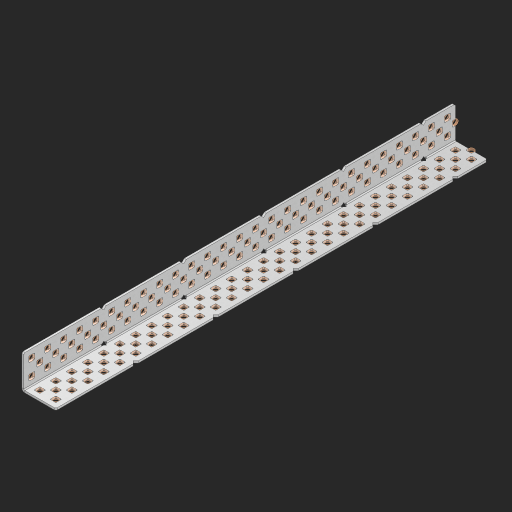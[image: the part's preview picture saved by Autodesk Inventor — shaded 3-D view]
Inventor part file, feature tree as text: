
AUTODESK INVENTOR PART (.ipt)
format: ipt  version: 2023 (Build 270158000, 158)  size: 1,927,168 bytes
history: native  units: in
note: dims shown in document units (in); Inventor stores cm internally (conversion verified against a paired STEP export)
features: other x168, extrude x160, sheet_metal_op x8, sketch x7, pattern_linear x2, mirror x1, chamfer x1
ambient origin geometry x8: Origin, YZ Plane, XZ Plane, XY Plane, X Axis, Y Axis, Z Axis, Center Point
bodies: Solid1 (feature_tree), Body (feature_tree)
feature tree (347):
  sheet_metal_op  "Flanges"
  sheet_metal_op  "Body Pattern"
  pattern_linear  "Center Pattern"  Spacing1=1.0in  [1 undecoded]
  other  "Arc Length"
  pattern_linear  "Notch Pattern"  Spacing1=0.25in  [1 undecoded]
  other  "Diagonal Plane"
  mirror  "Everything Mirrored"
  chamfer  "End Chamfer"
  sketch  "Sketch1"  dims[d0=1.0in]
  other  "Plate1"
  sketch  "Sketch2"  dims[d1=13.5in]
  other  "Plate2"
  sheet_metal_op  "Bend1"
  sheet_metal_op  "Corner1"
  sketch  "Sketch8"  dims[d2=0.0625in]
  sketch  "Sketch9"  dims[d3=0.0625in]
  other  "Srf91"
  sheet_metal_op  "Body Pattern Sketch"
  other  "Srf92"
  sketch  "Sketch13"  dims[d4=0.0312in]
  sketch  "Sketch15"  dims[d5=0.125in]
  sketch  "Sketch16"  dims[d6=0.0625in d7=1.0in d8=90.0deg d9=0.0312in d10=0.25in d11=0.0625in d12=0.0625in d49=0.182in d50=0.02in d52=0.25in d53=0.0625in d54=0.0in d55=0.172in d56=1.0in d57=0.0in d60=10.6299in d62=0.5in d63=0.7874in d65=0.5in d85=0.1473in d86=0.1782in d89=0.0625in d90=0.0in d91=0.04in d92=0.0491in d95=2.5in d96=0.04in d97=0.25in d98=45.0deg d99=0.25in d106=0.182in d107=0.02in d108=0.5in d110=0.0625in d111=0.0in d112=0.172in d113=0.5in d114=0.0in d117=0.5in d123=0.25in d125=0.25in d126=0.0491in d127=0.1473in d128=0.08in d129=0.04in d130=2.5in]
  other  "Srf786"
  other  "Srf856"
  other  "Srf857"
  other  "Srf858"
  other  "Srf859"
  other  "Srf860"
  other  "Srf861"
  other  "Srf889"
  other  "Srf890"
  other  "Srf891"
  other  "Srf1275"
  other  "Srf1276"
  other  "Srf1278"
  other  "Srf1279"
  other  "Srf1280"
  other  "Srf1281"
  other  "Srf1282"
  other  "Srf1283"
  other  "Srf1277"
  other  "Srf1285"
  other  "Srf1286"
  other  "Srf1287"
  other  "Srf1383"
  other  "Srf1384"
  other  "Srf1385"
  other  "Srf1386"
  other  "Srf1387"
  other  "Srf1388"
  other  "Srf1389"
  other  "Srf1390"
  other  "Srf1391"
  other  "Srf1392"
  other  "Srf1393"
  other  "Srf1394"
  other  "Srf1395"
  other  "Srf1396"
  other  "Srf1397"
  other  "Srf1398"
  other  "Srf1399"
  other  "Srf1400"
  other  "Srf1401"
  other  "Srf1402"
  other  "Srf1403"
  other  "Srf1404"
  other  "Srf1405"
  other  "Srf1406"
  other  "Srf1407"
  other  "Srf1408"
  other  "Srf1409"
  other  "Srf1410"
  other  "Srf1411"
  other  "Srf1412"
  other  "Srf1413"
  other  "Srf1414"
  other  "Srf1415"
  other  "Srf1416"
  other  "Srf1417"
  other  "Srf1418"
  other  "Srf1419"
  other  "Srf1420"
  other  "Srf1421"
  other  "Srf1422"
  other  "Srf1423"
  other  "Srf1424"
  other  "Srf1425"
  other  "Srf1426"
  other  "Srf1427"
  other  "Srf1428"
  other  "Srf1445"
  other  "Srf1446"
  other  "Srf1447"
  other  "Srf1448"
  other  "Srf1449"
  other  "Srf1450"
  other  "Srf1451"
  other  "Srf1452"
  other  "Srf1453"
  other  "Srf1454"
  other  "Srf1455"
  other  "Srf1456"
  other  "Srf1457"
  other  "Srf1458"
  other  "Srf1459"
  other  "Srf1460"
  other  "Srf1461"
  other  "Srf1462"
  other  "Srf1463"
  other  "Srf1464"
  other  "Srf1465"
  other  "Srf1466"
  other  "Srf1467"
  other  "Srf1475"
  other  "Srf1476"
  other  "Srf1477"
  other  "Srf1478"
  other  "Srf1479"
  other  "Srf1480"
  other  "Srf1481"
  other  "Srf1482"
  other  "Srf1483"
  other  "Srf1484"
  other  "Srf1485"
  other  "Srf1486"
  other  "Srf1487"
  other  "Srf1488"
  other  "Srf1489"
  other  "Srf1490"
  other  "Srf1491"
  other  "Srf1492"
  other  "Srf1493"
  other  "Srf1494"
  other  "Srf1495"
  other  "Srf1496"
  other  "Srf1497"
  other  "Srf1498"
  other  "Srf1499"
  other  "Srf1500"
  other  "Srf1501"
  other  "Srf1502"
  other  "Srf1503"
  other  "Srf1504"
  other  "Srf1505"
  other  "Srf1506"
  other  "Srf1507"
  other  "Srf1508"
  other  "Srf1509"
  other  "Srf1510"
  other  "Srf1511"
  other  "Srf1512"
  other  "Srf1513"
  other  "Srf1514"
  other  "Srf1515"
  other  "Srf1516"
  other  "Srf1517"
  other  "Srf1518"
  other  "Srf1519"
  other  "Srf1520"
  other  "Srf1537"
  other  "Srf1538"
  other  "Srf1539"
  other  "Srf1540"
  other  "Srf1541"
  other  "Srf1542"
  other  "Srf1543"
  other  "Srf1544"
  other  "Srf1545"
  other  "Srf1546"
  other  "Srf1547"
  other  "Srf1548"
  other  "Srf1549"
  other  "Srf1550"
  other  "Srf1551"
  other  "Srf1552"
  other  "Srf1553"
  other  "Srf1554"
  other  "Srf1555"
  other  "Srf1556"
  other  "Srf1557"
  other  "Srf1558"
  other  "Srf1559"
  sheet_metal_op  "Body Stamp"
  sheet_metal_op  "Body Circle"
  other  "Center Stamp"
  other  "Center Circle"
  sheet_metal_op  "Notch"
  extrude  "ExtrusionSrf92"  Depth=0.0625in
  extrude  "ExtrusionSrf856"  Depth=0.0625in
  extrude  "ExtrusionSrf857"  Depth=0.182in
  extrude  "ExtrusionSrf858"  Depth=0.02in
  extrude  "ExtrusionSrf859"  Depth=0.25in
  extrude  "ExtrusionSrf860"  Depth=0.0625in
  extrude  "ExtrusionSrf861"  TaperAngle=0.0deg  [1 undecoded]
  extrude  "ExtrusionSrf889"  Depth=2.5in
  extrude  "ExtrusionSrf890"  Depth=1.0in TaperAngle=0.0deg
  extrude  "ExtrusionSrf891"  Depth=2.5in
  extrude  "ExtrusionSrf1275"  Depth=0.5in
  extrude  "ExtrusionSrf1276"  Depth=2.5in
  extrude  "ExtrusionSrf1277"  Depth=2.5in
  extrude  "ExtrusionSrf1278"  Depth=0.0625in
  extrude  "ExtrusionSrf1279"  Depth=2.5in TaperAngle=0.0deg
  extrude  "ExtrusionSrf1280"  Depth=2.5in
  extrude  "ExtrusionSrf1281"  Depth=0.25in TaperAngle=45.0deg
  extrude  "ExtrusionSrf1282"  Depth=0.25in
  extrude  "ExtrusionSrf1345"  Depth=0.182in
  extrude  "ExtrusionSrf1346"  Depth=0.02in
  extrude  "ExtrusionSrf1347"  Depth=0.5in
  extrude  "ExtrusionSrf1348"  Depth=0.0625in
  extrude  "ExtrusionSrf1383"  TaperAngle=0.0deg  [1 undecoded]
  extrude  "ExtrusionSrf1384"  Depth=2.5in
  extrude  "ExtrusionSrf1385"  Depth=0.5in TaperAngle=0.0deg
  extrude  "ExtrusionSrf1386"  Depth=0.5in
  extrude  "ExtrusionSrf1387"  Depth=0.25in
  extrude  "ExtrusionSrf1388"  Depth=0.25in
  extrude  "ExtrusionSrf1389"  Depth=2.5in
  extrude  "ExtrusionSrf1390"  Depth=2.5in
  extrude  "ExtrusionSrf1391"  Depth=2.5in
  extrude  "ExtrusionSrf1392"  Depth=2.5in
  extrude  "ExtrusionSrf1393"  Depth=2.5in
  extrude  "ExtrusionSrf1394"  [1 undecoded]
  extrude  "ExtrusionSrf1395"  [1 undecoded]
  extrude  "ExtrusionSrf1396"  [1 undecoded]
  extrude  "ExtrusionSrf1397"  [1 undecoded]
  extrude  "ExtrusionSrf1398"  [1 undecoded]
  extrude  "ExtrusionSrf1399"  [1 undecoded]
  extrude  "ExtrusionSrf1400"  [1 undecoded]
  extrude  "ExtrusionSrf1401"  [1 undecoded]
  extrude  "ExtrusionSrf1402"  [1 undecoded]
  extrude  "ExtrusionSrf1403"  [1 undecoded]
  extrude  "ExtrusionSrf1404"  [1 undecoded]
  extrude  "ExtrusionSrf1405"  [1 undecoded]
  extrude  "ExtrusionSrf1406"  [1 undecoded]
  extrude  "ExtrusionSrf1407"  [1 undecoded]
  extrude  "ExtrusionSrf1408"  [1 undecoded]
  extrude  "ExtrusionSrf1409"  [1 undecoded]
  extrude  "ExtrusionSrf1410"  [1 undecoded]
  extrude  "ExtrusionSrf1411"  [1 undecoded]
  extrude  "ExtrusionSrf1412"  [1 undecoded]
  extrude  "ExtrusionSrf1413"  [1 undecoded]
  extrude  "ExtrusionSrf1414"  [1 undecoded]
  extrude  "ExtrusionSrf1415"  [1 undecoded]
  extrude  "ExtrusionSrf1416"  [1 undecoded]
  extrude  "ExtrusionSrf1417"  [1 undecoded]
  extrude  "ExtrusionSrf1418"  [1 undecoded]
  extrude  "ExtrusionSrf1419"  [1 undecoded]
  extrude  "ExtrusionSrf1420"  [1 undecoded]
  extrude  "ExtrusionSrf1421"  [1 undecoded]
  extrude  "ExtrusionSrf1422"  [1 undecoded]
  extrude  "ExtrusionSrf1423"  [1 undecoded]
  extrude  "ExtrusionSrf1424"  [1 undecoded]
  extrude  "ExtrusionSrf1425"  [1 undecoded]
  extrude  "ExtrusionSrf1426"  [1 undecoded]
  extrude  "ExtrusionSrf1427"  [1 undecoded]
  extrude  "ExtrusionSrf1428"  [1 undecoded]
  extrude  "ExtrusionSrf1445"  [1 undecoded]
  extrude  "ExtrusionSrf1446"  [1 undecoded]
  extrude  "ExtrusionSrf1447"  [1 undecoded]
  extrude  "ExtrusionSrf1448"  [1 undecoded]
  extrude  "ExtrusionSrf1449"  [1 undecoded]
  extrude  "ExtrusionSrf1450"  [1 undecoded]
  extrude  "ExtrusionSrf1451"  [1 undecoded]
  extrude  "ExtrusionSrf1452"  [1 undecoded]
  extrude  "ExtrusionSrf1453"  [1 undecoded]
  extrude  "ExtrusionSrf1454"  [1 undecoded]
  extrude  "ExtrusionSrf1455"  [1 undecoded]
  extrude  "ExtrusionSrf1456"  [1 undecoded]
  extrude  "ExtrusionSrf1457"  [1 undecoded]
  extrude  "ExtrusionSrf1458"  [1 undecoded]
  extrude  "ExtrusionSrf1459"  [1 undecoded]
  extrude  "ExtrusionSrf1460"  [1 undecoded]
  extrude  "ExtrusionSrf1461"  [1 undecoded]
  extrude  "ExtrusionSrf1462"  [1 undecoded]
  extrude  "ExtrusionSrf1463"  [1 undecoded]
  extrude  "ExtrusionSrf1464"  [1 undecoded]
  extrude  "ExtrusionSrf1465"  [1 undecoded]
  extrude  "ExtrusionSrf1466"  [1 undecoded]
  extrude  "ExtrusionSrf1467"  [1 undecoded]
  extrude  "ExtrusionSrf1475"  [1 undecoded]
  extrude  "ExtrusionSrf1476"  [1 undecoded]
  extrude  "ExtrusionSrf1477"  [1 undecoded]
  extrude  "ExtrusionSrf1478"  [1 undecoded]
  extrude  "ExtrusionSrf1479"  [1 undecoded]
  extrude  "ExtrusionSrf1480"  [1 undecoded]
  extrude  "ExtrusionSrf1481"  [1 undecoded]
  extrude  "ExtrusionSrf1482"  [1 undecoded]
  extrude  "ExtrusionSrf1483"  [1 undecoded]
  extrude  "ExtrusionSrf1484"  [1 undecoded]
  extrude  "ExtrusionSrf1485"  [1 undecoded]
  extrude  "ExtrusionSrf1486"  [1 undecoded]
  extrude  "ExtrusionSrf1487"  [1 undecoded]
  extrude  "ExtrusionSrf1488"  [1 undecoded]
  extrude  "ExtrusionSrf1489"  [1 undecoded]
  extrude  "ExtrusionSrf1490"  [1 undecoded]
  extrude  "ExtrusionSrf1491"  [1 undecoded]
  extrude  "ExtrusionSrf1492"  [1 undecoded]
  extrude  "ExtrusionSrf1493"  [1 undecoded]
  extrude  "ExtrusionSrf1494"  [1 undecoded]
  extrude  "ExtrusionSrf1495"  [1 undecoded]
  extrude  "ExtrusionSrf1496"  [1 undecoded]
  extrude  "ExtrusionSrf1497"  [1 undecoded]
  extrude  "ExtrusionSrf1498"  [1 undecoded]
  extrude  "ExtrusionSrf1499"  [1 undecoded]
  extrude  "ExtrusionSrf1500"  [1 undecoded]
  extrude  "ExtrusionSrf1501"  [1 undecoded]
  extrude  "ExtrusionSrf1502"  [1 undecoded]
  extrude  "ExtrusionSrf1503"  [1 undecoded]
  extrude  "ExtrusionSrf1504"  [1 undecoded]
  extrude  "ExtrusionSrf1505"  [1 undecoded]
  extrude  "ExtrusionSrf1506"  [1 undecoded]
  extrude  "ExtrusionSrf1507"  [1 undecoded]
  extrude  "ExtrusionSrf1508"  [1 undecoded]
  extrude  "ExtrusionSrf1509"  [1 undecoded]
  extrude  "ExtrusionSrf1510"  [1 undecoded]
  extrude  "ExtrusionSrf1511"  [1 undecoded]
  extrude  "ExtrusionSrf1512"  [1 undecoded]
  extrude  "ExtrusionSrf1513"  [1 undecoded]
  extrude  "ExtrusionSrf1514"  [1 undecoded]
  extrude  "ExtrusionSrf1515"  [1 undecoded]
  extrude  "ExtrusionSrf1516"  [1 undecoded]
  extrude  "ExtrusionSrf1517"  [1 undecoded]
  extrude  "ExtrusionSrf1518"  [1 undecoded]
  extrude  "ExtrusionSrf1519"  [1 undecoded]
  extrude  "ExtrusionSrf1520"  [1 undecoded]
  extrude  "ExtrusionSrf1537"  [1 undecoded]
  extrude  "ExtrusionSrf1538"  [1 undecoded]
  extrude  "ExtrusionSrf1539"  [1 undecoded]
  extrude  "ExtrusionSrf1540"  [1 undecoded]
  extrude  "ExtrusionSrf1541"  [1 undecoded]
  extrude  "ExtrusionSrf1542"  [1 undecoded]
  extrude  "ExtrusionSrf1543"  [1 undecoded]
  extrude  "ExtrusionSrf1544"  [1 undecoded]
  extrude  "ExtrusionSrf1545"  [1 undecoded]
  extrude  "ExtrusionSrf1546"  [1 undecoded]
  extrude  "ExtrusionSrf1547"  [1 undecoded]
  extrude  "ExtrusionSrf1548"  [1 undecoded]
  extrude  "ExtrusionSrf1549"  [1 undecoded]
  extrude  "ExtrusionSrf1550"  [1 undecoded]
  extrude  "ExtrusionSrf1551"  [1 undecoded]
  extrude  "ExtrusionSrf1552"  [1 undecoded]
  extrude  "ExtrusionSrf1553"  [1 undecoded]
  extrude  "ExtrusionSrf1554"  [1 undecoded]
  extrude  "ExtrusionSrf1555"  [1 undecoded]
  extrude  "ExtrusionSrf1556"  [1 undecoded]
  extrude  "ExtrusionSrf1557"  [1 undecoded]
  extrude  "ExtrusionSrf1558"  [1 undecoded]
  extrude  "ExtrusionSrf1559"  [1 undecoded]
note: 131 required parameter values undecoded (feature->parameter linkage not recoverable at this tier; creation-order binding heuristic only, values carry confidence <= 0.55)
